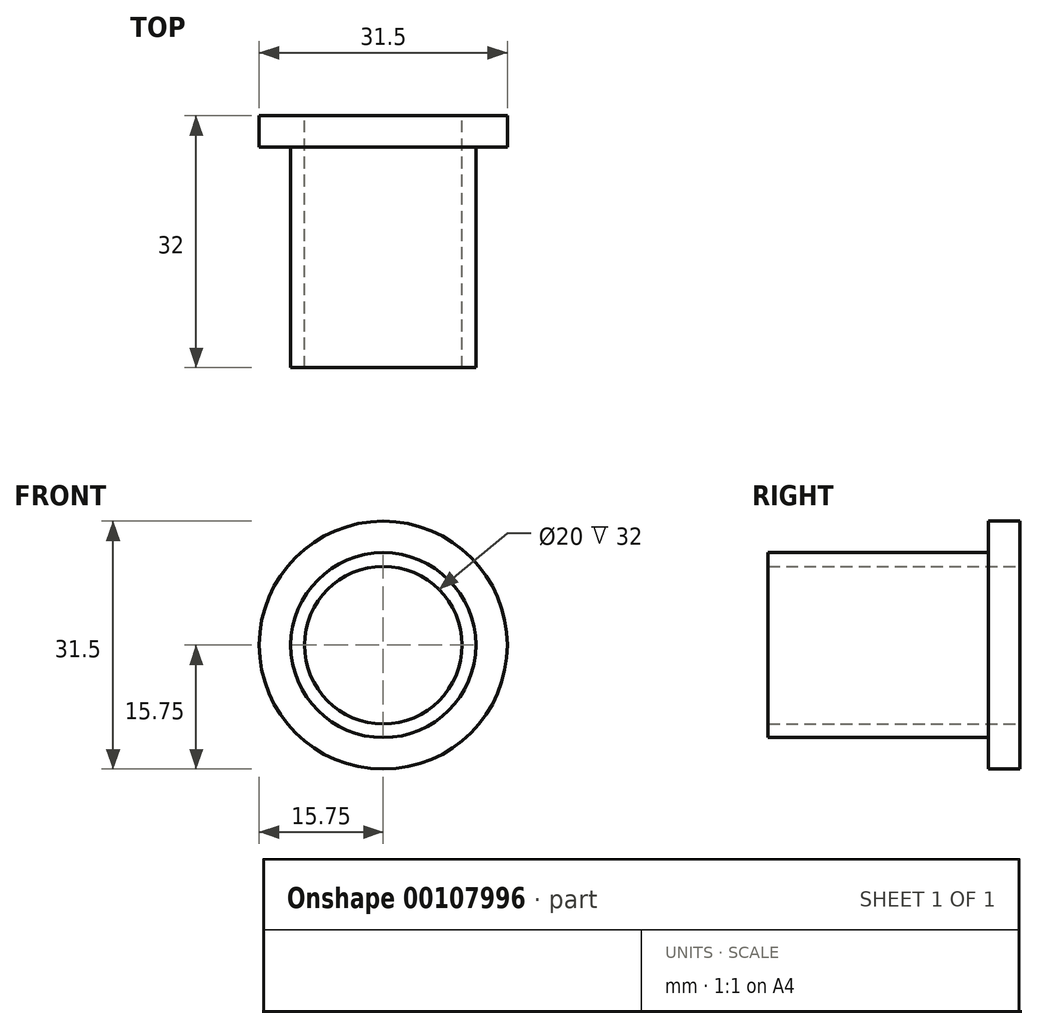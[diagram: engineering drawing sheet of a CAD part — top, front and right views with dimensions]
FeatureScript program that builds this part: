
annotation { "Feature Type Name" : "Feature", "Feature Type Description" : "" }
export const myFeature = defineFeature(function(context is Context, id is Id, definition is map)
    precondition{}
    {
        {
            var Q0;
            Q0=qCreatedBy(makeId("Front.planeOp"),FACE);
            var sketch = newSketch(context, id + "F0", { "sketchPlane" : qUnion([Q0])});
            skCircle(sketch, "E0", {"center": v(0, 0) * mm, "radius": 15.75 * mm});
            skCircle(sketch, "E1", {"center": v(0, 0) * mm, "radius": 11.75 * mm});
            skCircle(sketch, "E2", {"center": v(0, 0) * mm, "radius": 10 * mm});
            skSolve(sketch);
        }
        {
            var Q0;
            Q0 = qSketchRegion(id + "F0", true);
            var Q1;
            Q1=makeQuery(id+"F0.imprint","IMPRINT",FACE,{"disambiguationData":[TD([[makeQuery(id+"F0.imprint","IMPRINT",EDGE,{"derivedFrom":sQuery(id+"F0.wireOp",EDGE,"E1")}),1.0]])]});
            extrude(context, id + "F1", {"entities" : qUnion([Q0, Q1]), "depth" : 4 * mm});
        }
        {
            var Q0;
            Q0=makeQuery(id+"F0.imprint","IMPRINT",FACE,{"disambiguationData":[TD([[makeQuery(id+"F0.imprint","IMPRINT",EDGE,{"derivedFrom":sQuery(id+"F0.wireOp",EDGE,"E1")}),1.0]])]});
            extrude(context, id + "F2", {"entities" : qUnion([Q0]), "operationType" : NewBodyOperationType.ADD, "depth" : 32 * mm});
        }
    });
